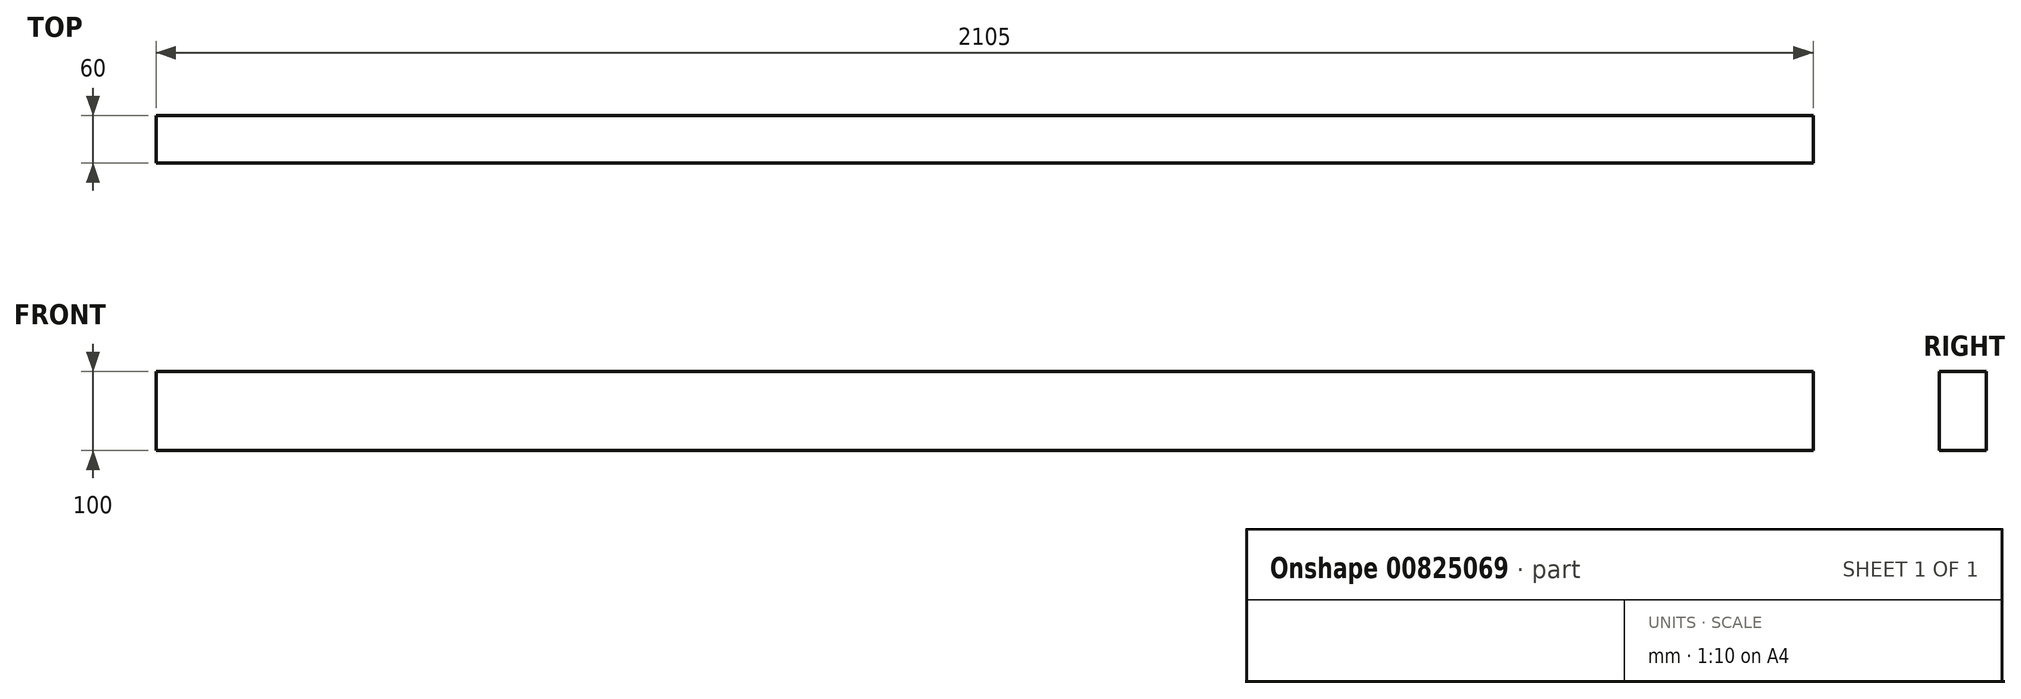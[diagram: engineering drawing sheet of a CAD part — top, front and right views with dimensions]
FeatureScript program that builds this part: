
annotation { "Feature Type Name" : "Feature", "Feature Type Description" : "" }
export const myFeature = defineFeature(function(context is Context, id is Id, definition is map)
    precondition{}
    {
        {
            var Q0;
            Q0=qCreatedBy(makeId("Top.planeOp"),FACE);
            var sketch = newSketch(context, id + "F0", { "sketchPlane" : qUnion([Q0])});
            skLineSegment(sketch, "E0.bottom", {"start": v(-1054.97, 17.74) * mm, "end": v(1050.03, 17.74) * mm});
            skLineSegment(sketch, "E0.top", {"start": v(-1054.97, -42.26) * mm, "end": v(1050.03, -42.26) * mm});
            skLineSegment(sketch, "E0.left", {"start": v(-1054.97, 17.74) * mm, "end": v(-1054.97, -42.26) * mm});
            skLineSegment(sketch, "E0.right", {"start": v(1050.03, 17.74) * mm, "end": v(1050.03, -42.26) * mm});
            skSolve(sketch);
        }
        {
            var Q0;
            Q0 = qSketchRegion(id + "F0", true);
            extrude(context, id + "F1", {"entities" : qUnion([Q0]), "depth" : 100 * mm, "offsetDistance" : 25 * mm});
        }
    });
